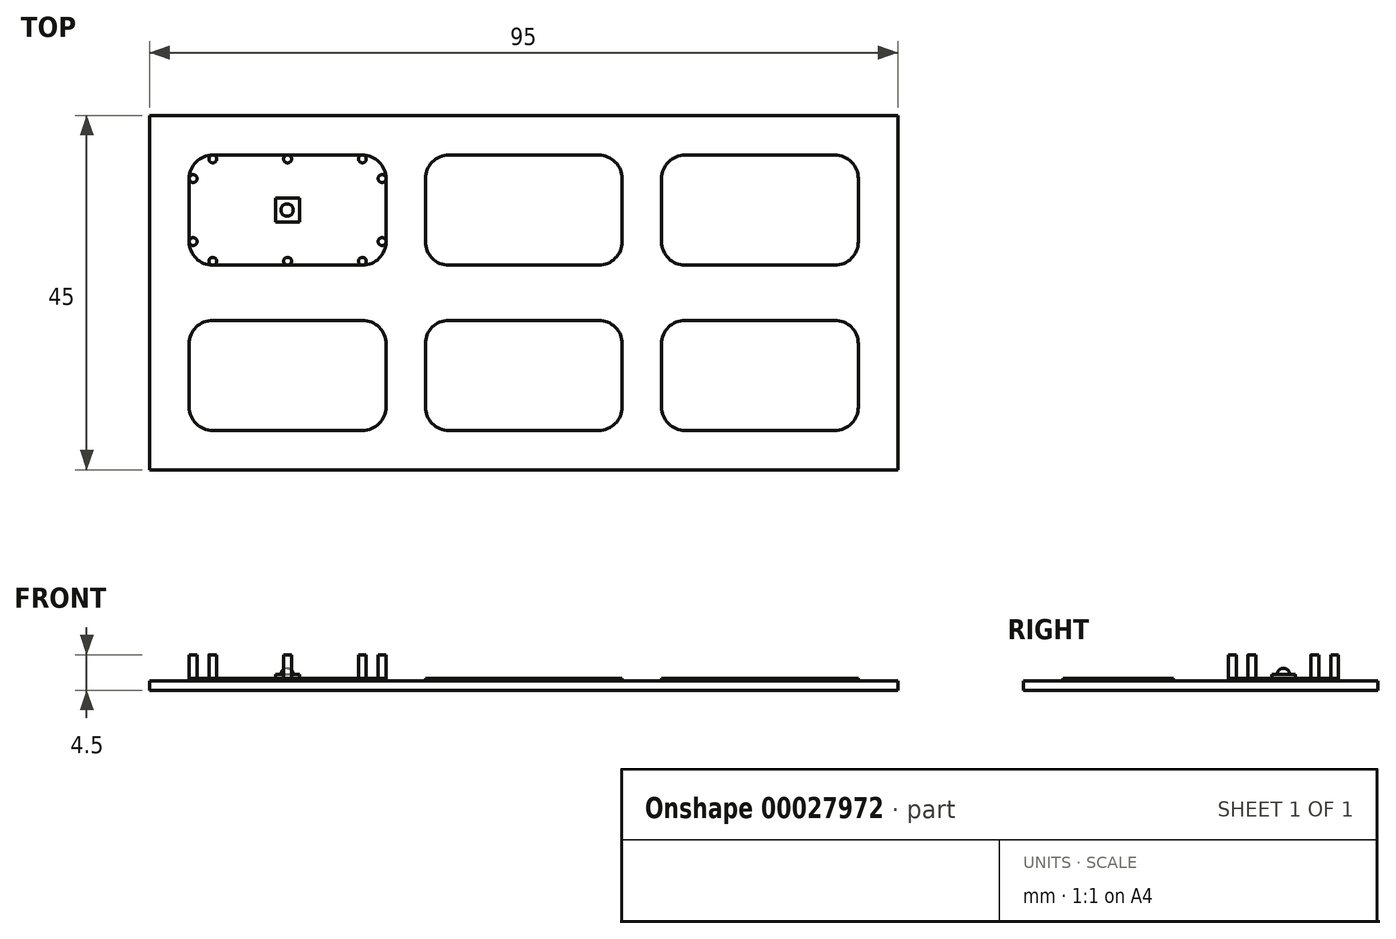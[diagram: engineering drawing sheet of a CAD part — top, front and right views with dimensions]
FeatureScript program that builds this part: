
annotation { "Feature Type Name" : "Feature", "Feature Type Description" : "" }
export const myFeature = defineFeature(function(context is Context, id is Id, definition is map)
    precondition{}
    {
        {
            var Q0;
            Q0=qCreatedBy(makeId("Top.planeOp"),FACE);
            var sketch = newSketch(context, id + "F0", { "sketchPlane" : qUnion([Q0])});
            skLineSegment(sketch, "E0.bottom", {"start": v(0, 0) * mm, "end": v(95, 0) * mm});
            skLineSegment(sketch, "E0.top", {"start": v(0, -45) * mm, "end": v(95, -45) * mm});
            skLineSegment(sketch, "E0.left", {"start": v(0, 0) * mm, "end": v(0, -45) * mm});
            skLineSegment(sketch, "E0.right", {"start": v(95, 0) * mm, "end": v(95, -45) * mm});
            skSolve(sketch);
        }
        {
            var Q0;
            Q0 = qSketchRegion(id + "F0", true);
            extrude(context, id + "F1", {"entities" : qUnion([Q0]), "depth" : 1.2 * mm});
        }
        {
            var Q0;
            Q0=makeQuery(id+"F1.opExtrude","CAP_FACE",FACE,{"disambiguationData":[OSD([sQuery(id+"F0.wireOp",EDGE,"E0.bottom"),sQuery(id+"F0.wireOp",EDGE,"E0.top"),sQuery(id+"F0.wireOp",EDGE,"E0.left"),sQuery(id+"F0.wireOp",EDGE,"E0.right")])],"isStart":false});
            var sketch = newSketch(context, id + "F2", { "sketchPlane" : qUnion([Q0])});
            skLineSegment(sketch, "E1.bottom", {"start": v(8, -5) * mm, "end": v(27, -5) * mm});
            skLineSegment(sketch, "E1.top", {"start": v(8, -19) * mm, "end": v(27, -19) * mm});
            skLineSegment(sketch, "E1.left", {"start": v(5, -8) * mm, "end": v(5, -16) * mm});
            skLineSegment(sketch, "E1.right", {"start": v(30, -8) * mm, "end": v(30, -16) * mm});
            skPoint(sketch, "E2.visualSharp", {"position": v(5, -5) * mm});
            skArc(sketch, "E2.filletArc", {"start": v(8, -5) * mm, "mid": v(5.88, -5.88) * mm, "end": v(5, -8) * mm});
            skPoint(sketch, "E3.visualSharp", {"position": v(5, -19) * mm});
            skArc(sketch, "E3.filletArc", {"start": v(5, -16) * mm, "mid": v(5.88, -18.12) * mm, "end": v(8, -19) * mm});
            skPoint(sketch, "E4.visualSharp", {"position": v(30, -19) * mm});
            skArc(sketch, "E4.filletArc", {"start": v(27, -19) * mm, "mid": v(29.12, -18.12) * mm, "end": v(30, -16) * mm});
            skPoint(sketch, "E5.visualSharp", {"position": v(30, -5) * mm});
            skArc(sketch, "E5.filletArc", {"start": v(30, -8) * mm, "mid": v(29.12, -5.88) * mm, "end": v(27, -5) * mm});
            skPoint(sketch, "E6.0.1.0", {"position": v(30, -26) * mm});
            skPoint(sketch, "E6.0.1.1", {"position": v(30, -40) * mm});
            skPoint(sketch, "E6.0.1.2", {"position": v(5, -26) * mm});
            skLineSegment(sketch, "E6.0.1.3", {"start": v(8, -26) * mm, "end": v(27, -26) * mm});
            skLineSegment(sketch, "E6.0.1.4", {"start": v(5, -29) * mm, "end": v(5, -37) * mm});
            skLineSegment(sketch, "E6.0.1.5", {"start": v(30, -29) * mm, "end": v(30, -37) * mm});
            skLineSegment(sketch, "E6.0.1.6", {"start": v(8, -40) * mm, "end": v(27, -40) * mm});
            skArc(sketch, "E6.0.1.7", {"start": v(30, -29) * mm, "mid": v(29.12, -26.88) * mm, "end": v(27, -26) * mm});
            skArc(sketch, "E6.0.1.8", {"start": v(8, -26) * mm, "mid": v(5.88, -26.88) * mm, "end": v(5, -29) * mm});
            skArc(sketch, "E6.0.1.9", {"start": v(5, -37) * mm, "mid": v(5.88, -39.12) * mm, "end": v(8, -40) * mm});
            skArc(sketch, "E6.0.1.10", {"start": v(27, -40) * mm, "mid": v(29.12, -39.12) * mm, "end": v(30, -37) * mm});
            skPoint(sketch, "E6.0.1.11", {"position": v(5, -40) * mm});
            skPoint(sketch, "E6.1.0.0", {"position": v(60, -5) * mm});
            skPoint(sketch, "E6.1.0.1", {"position": v(60, -19) * mm});
            skPoint(sketch, "E6.1.0.2", {"position": v(35, -5) * mm});
            skLineSegment(sketch, "E6.1.0.3", {"start": v(38, -5) * mm, "end": v(57, -5) * mm});
            skLineSegment(sketch, "E6.1.0.4", {"start": v(35, -8) * mm, "end": v(35, -16) * mm});
            skLineSegment(sketch, "E6.1.0.5", {"start": v(60, -8) * mm, "end": v(60, -16) * mm});
            skLineSegment(sketch, "E6.1.0.6", {"start": v(38, -19) * mm, "end": v(57, -19) * mm});
            skArc(sketch, "E6.1.0.7", {"start": v(60, -8) * mm, "mid": v(59.12, -5.88) * mm, "end": v(57, -5) * mm});
            skArc(sketch, "E6.1.0.8", {"start": v(38, -5) * mm, "mid": v(35.88, -5.88) * mm, "end": v(35, -8) * mm});
            skArc(sketch, "E6.1.0.9", {"start": v(35, -16) * mm, "mid": v(35.88, -18.12) * mm, "end": v(38, -19) * mm});
            skArc(sketch, "E6.1.0.10", {"start": v(57, -19) * mm, "mid": v(59.12, -18.12) * mm, "end": v(60, -16) * mm});
            skPoint(sketch, "E6.1.0.11", {"position": v(35, -19) * mm});
            skPoint(sketch, "E6.1.1.0", {"position": v(60, -26) * mm});
            skPoint(sketch, "E6.1.1.1", {"position": v(60, -40) * mm});
            skPoint(sketch, "E6.1.1.2", {"position": v(35, -26) * mm});
            skLineSegment(sketch, "E6.1.1.3", {"start": v(38, -26) * mm, "end": v(57, -26) * mm});
            skLineSegment(sketch, "E6.1.1.4", {"start": v(35, -29) * mm, "end": v(35, -37) * mm});
            skLineSegment(sketch, "E6.1.1.5", {"start": v(60, -29) * mm, "end": v(60, -37) * mm});
            skLineSegment(sketch, "E6.1.1.6", {"start": v(38, -40) * mm, "end": v(57, -40) * mm});
            skArc(sketch, "E6.1.1.7", {"start": v(60, -29) * mm, "mid": v(59.12, -26.88) * mm, "end": v(57, -26) * mm});
            skArc(sketch, "E6.1.1.8", {"start": v(38, -26) * mm, "mid": v(35.88, -26.88) * mm, "end": v(35, -29) * mm});
            skArc(sketch, "E6.1.1.9", {"start": v(35, -37) * mm, "mid": v(35.88, -39.12) * mm, "end": v(38, -40) * mm});
            skArc(sketch, "E6.1.1.10", {"start": v(57, -40) * mm, "mid": v(59.12, -39.12) * mm, "end": v(60, -37) * mm});
            skPoint(sketch, "E6.1.1.11", {"position": v(35, -40) * mm});
            skPoint(sketch, "E6.2.0.0", {"position": v(90, -5) * mm});
            skPoint(sketch, "E6.2.0.1", {"position": v(90, -19) * mm});
            skPoint(sketch, "E6.2.0.2", {"position": v(65, -5) * mm});
            skLineSegment(sketch, "E6.2.0.3", {"start": v(68, -5) * mm, "end": v(87, -5) * mm});
            skLineSegment(sketch, "E6.2.0.4", {"start": v(65, -8) * mm, "end": v(65, -16) * mm});
            skLineSegment(sketch, "E6.2.0.5", {"start": v(90, -8) * mm, "end": v(90, -16) * mm});
            skLineSegment(sketch, "E6.2.0.6", {"start": v(68, -19) * mm, "end": v(87, -19) * mm});
            skArc(sketch, "E6.2.0.7", {"start": v(90, -8) * mm, "mid": v(89.12, -5.88) * mm, "end": v(87, -5) * mm});
            skArc(sketch, "E6.2.0.8", {"start": v(68, -5) * mm, "mid": v(65.88, -5.88) * mm, "end": v(65, -8) * mm});
            skArc(sketch, "E6.2.0.9", {"start": v(65, -16) * mm, "mid": v(65.88, -18.12) * mm, "end": v(68, -19) * mm});
            skArc(sketch, "E6.2.0.10", {"start": v(87, -19) * mm, "mid": v(89.12, -18.12) * mm, "end": v(90, -16) * mm});
            skPoint(sketch, "E6.2.0.11", {"position": v(65, -19) * mm});
            skPoint(sketch, "E6.2.1.0", {"position": v(90, -26) * mm});
            skPoint(sketch, "E6.2.1.1", {"position": v(90, -40) * mm});
            skPoint(sketch, "E6.2.1.2", {"position": v(65, -26) * mm});
            skLineSegment(sketch, "E6.2.1.3", {"start": v(68, -26) * mm, "end": v(87, -26) * mm});
            skLineSegment(sketch, "E6.2.1.4", {"start": v(65, -29) * mm, "end": v(65, -37) * mm});
            skLineSegment(sketch, "E6.2.1.5", {"start": v(90, -29) * mm, "end": v(90, -37) * mm});
            skLineSegment(sketch, "E6.2.1.6", {"start": v(68, -40) * mm, "end": v(87, -40) * mm});
            skArc(sketch, "E6.2.1.7", {"start": v(90, -29) * mm, "mid": v(89.12, -26.88) * mm, "end": v(87, -26) * mm});
            skArc(sketch, "E6.2.1.8", {"start": v(68, -26) * mm, "mid": v(65.88, -26.88) * mm, "end": v(65, -29) * mm});
            skArc(sketch, "E6.2.1.9", {"start": v(65, -37) * mm, "mid": v(65.88, -39.12) * mm, "end": v(68, -40) * mm});
            skArc(sketch, "E6.2.1.10", {"start": v(87, -40) * mm, "mid": v(89.12, -39.12) * mm, "end": v(90, -37) * mm});
            skPoint(sketch, "E6.2.1.11", {"position": v(65, -40) * mm});
            skLineSegment(sketch, "E6.direction1", {"start": v(30, -5) * mm, "end": v(60, -5) * mm, "construction": true});
            skLineSegment(sketch, "E6.direction2", {"start": v(30, -5) * mm, "end": v(30, -26) * mm, "construction": true});
            skSolve(sketch);
        }
        {
            var Q0;
            Q0 = qSketchRegion(id + "F2", true);
            extrude(context, id + "F3", {"entities" : qUnion([Q0]), "operationType" : NewBodyOperationType.ADD, "depth" : .3 * mm});
        }
        {
            var Q0;
            Q0=makeQuery(id+"F3.opExtrude","CAP_FACE",FACE,{"disambiguationData":[OSD([sQuery(id+"F2.wireOp",EDGE,"E1.bottom"),sQuery(id+"F2.wireOp",EDGE,"E1.top"),sQuery(id+"F2.wireOp",EDGE,"E1.left"),sQuery(id+"F2.wireOp",EDGE,"E1.right"),sQuery(id+"F2.wireOp",EDGE,"E2.filletArc"),sQuery(id+"F2.wireOp",EDGE,"E3.filletArc"),sQuery(id+"F2.wireOp",EDGE,"E4.filletArc"),sQuery(id+"F2.wireOp",EDGE,"E5.filletArc")])],"isStart":false});
            var sketch = newSketch(context, id + "F4", { "sketchPlane" : qUnion([Q0])});
            skLineSegment(sketch, "E7.rect.bottom", {"start": v(19, -10.5) * mm, "end": v(16, -10.5) * mm});
            skLineSegment(sketch, "E7.rect.top", {"start": v(19, -13.5) * mm, "end": v(16, -13.5) * mm});
            skLineSegment(sketch, "E7.rect.left", {"start": v(19, -10.5) * mm, "end": v(19, -13.5) * mm});
            skLineSegment(sketch, "E7.rect.right", {"start": v(16, -10.5) * mm, "end": v(16, -13.5) * mm});
            skPoint(sketch, "E7.rect.middle", {"position": v(17.5, -12) * mm});
            skSolve(sketch);
        }
        {
            var Q0;
            Q0 = qSketchRegion(id + "F4", true);
            extrude(context, id + "F5", {"entities" : qUnion([Q0]), "operationType" : NewBodyOperationType.ADD, "depth" : .5 * mm});
        }
        {
            var Q0;
            Q0=qCreatedBy(makeId("Front.planeOp"),FACE);
            cPlane(context, id + "F6", {"entities" : qUnion([Q0]), "cplaneType" : CPlaneType.OFFSET, "offset" : 12 * mm, "width" : 150 * mm, "height" : 150 * mm});
        }
        {
            var Q0;
            Q0=qCreatedBy(id+"F6.planeOp",FACE);
            var sketch = newSketch(context, id + "F7", { "sketchPlane" : qUnion([Q0])});
            skLineSegment(sketch, "E8", {"start": v(17.44, 2) * mm, "end": v(16.65, 2) * mm});
            skLineSegment(sketch, "E9", {"start": v(17.44, 2) * mm, "end": v(17.44, 2.79) * mm});
            skArc(sketch, "E10", {"start": v(17.44, 2.79) * mm, "mid": v(16.88, 2.56) * mm, "end": v(16.65, 2) * mm});
            skSolve(sketch);
        }
        {
            var Q0;
            Q0 = qSketchRegion(id + "F7", true);
            var Q1;
            Q1=sQuery(id+"F7.wireOp",EDGE,"E9");
            revolve(context, id + "F8", {"operationType" : NewBodyOperationType.ADD, "entities" : qUnion([Q0]), "axis" : qUnion([Q1]), "revolveType" : RevolveType.FULL});
        }
        {
            var Q0;
            Q0=makeQuery(id+"F3.opExtrude","CAP_FACE",FACE,{"disambiguationData":[OSD([sQuery(id+"F2.wireOp",EDGE,"E1.bottom"),sQuery(id+"F2.wireOp",EDGE,"E1.top"),sQuery(id+"F2.wireOp",EDGE,"E1.left"),sQuery(id+"F2.wireOp",EDGE,"E1.right"),sQuery(id+"F2.wireOp",EDGE,"E2.filletArc"),sQuery(id+"F2.wireOp",EDGE,"E3.filletArc"),sQuery(id+"F2.wireOp",EDGE,"E4.filletArc"),sQuery(id+"F2.wireOp",EDGE,"E5.filletArc")])],"isStart":false});
            var sketch = newSketch(context, id + "F9", { "sketchPlane" : qUnion([Q0])});
            skCircle(sketch, "E11", {"center": v(8, -5.5) * mm, "radius": 0.5 * mm});
            skCircle(sketch, "E12", {"center": v(5.5, -8) * mm, "radius": 0.5 * mm});
            skCircle(sketch, "E13.0.1.0", {"center": v(8, -18.5) * mm, "radius": 0.5 * mm});
            skCircle(sketch, "E13.1.0.0", {"center": v(17.5, -5.5) * mm, "radius": 0.5 * mm});
            skCircle(sketch, "E13.1.1.0", {"center": v(17.5, -18.5) * mm, "radius": 0.5 * mm});
            skCircle(sketch, "E13.2.0.0", {"center": v(27, -5.5) * mm, "radius": 0.5 * mm});
            skCircle(sketch, "E13.2.1.0", {"center": v(27, -18.5) * mm, "radius": 0.5 * mm});
            skLineSegment(sketch, "E13.direction1", {"start": v(8, -5.5) * mm, "end": v(17.5, -5.5) * mm, "construction": true});
            skLineSegment(sketch, "E13.direction2", {"start": v(8, -5.5) * mm, "end": v(8, -18.5) * mm, "construction": true});
            skCircle(sketch, "E14.0.1.0", {"center": v(5.5, -16) * mm, "radius": 0.5 * mm});
            skCircle(sketch, "E14.1.0.0", {"center": v(29.5, -8) * mm, "radius": 0.5 * mm});
            skCircle(sketch, "E14.1.1.0", {"center": v(29.5, -16) * mm, "radius": 0.5 * mm});
            skLineSegment(sketch, "E14.direction1", {"start": v(5.5, -8) * mm, "end": v(29.5, -8) * mm, "construction": true});
            skLineSegment(sketch, "E14.direction2", {"start": v(5.5, -8) * mm, "end": v(5.5, -16) * mm, "construction": true});
            skSolve(sketch);
        }
        {
            var Q0;
            Q0 = qSketchRegion(id + "F9", true);
            extrude(context, id + "F10", {"entities" : qUnion([Q0]), "operationType" : NewBodyOperationType.ADD, "depth" : 3 * mm});
        }
    });
